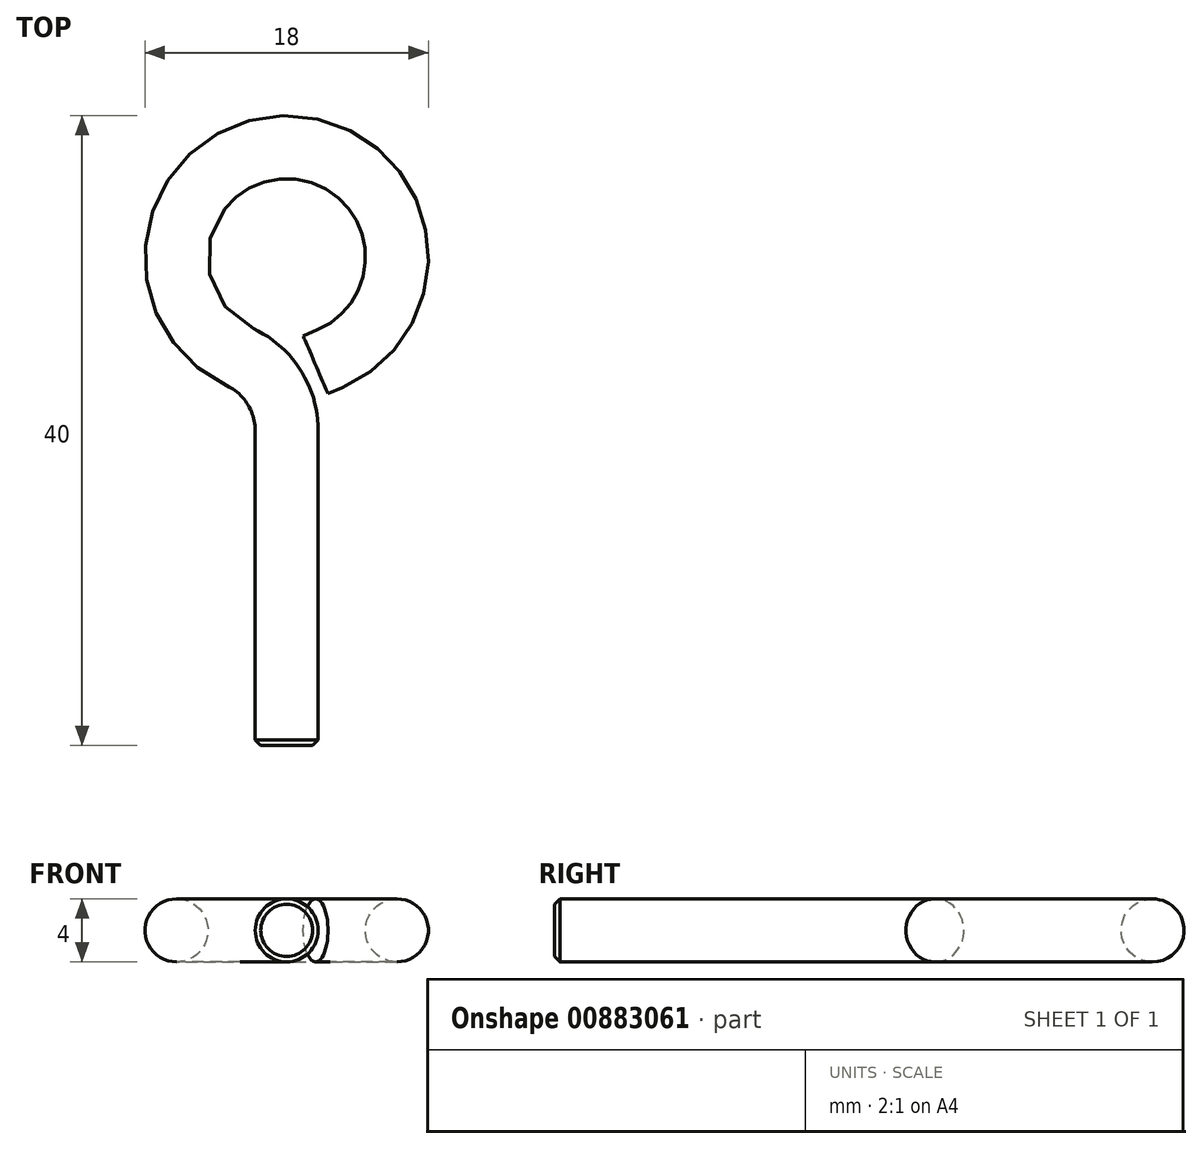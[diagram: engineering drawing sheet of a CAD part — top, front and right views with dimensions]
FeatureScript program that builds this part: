
annotation { "Feature Type Name" : "Feature", "Feature Type Description" : "" }
export const myFeature = defineFeature(function(context is Context, id is Id, definition is map)
    precondition{}
    {
        {
            var Q0;
            Q0=qCreatedBy(makeId("Top.planeOp"),FACE);
            var sketch = newSketch(context, id + "F0", { "sketchPlane" : qUnion([Q0])});
            skArc(sketch, "E0", {"start": v(2.76, 24.57) * mm, "mid": v(0.11, 38) * mm, "end": v(-2.96, 24.66) * mm});
            skLineSegment(sketch, "E1", {"start": v(0, 0) * mm, "end": v(0, 20) * mm});
            skArc(sketch, "E2", {"start": v(0, 20) * mm, "mid": v(-0.8, 22.76) * mm, "end": v(-2.96, 24.66) * mm});
            skLineSegment(sketch, "E3", {"start": v(2.76, 24.57) * mm, "end": v(1.84, 24.17) * mm});
            skSolve(sketch);
        }
        {
            var Q0;
            Q0=qCreatedBy(makeId("Front.planeOp"),FACE);
            var sketch = newSketch(context, id + "F1", { "sketchPlane" : qUnion([Q0])});
            skCircle(sketch, "E4", {"center": v(0, 0) * mm, "radius": 2 * mm});
            skSolve(sketch);
        }
        {
            var Q0;
            Q0=makeQuery(id+"F1.imprint","IMPRINT",FACE,{"disambiguationData":[TD([[makeQuery(id+"F1.imprint","IMPRINT",EDGE,{"derivedFrom":sQuery(id+"F1.wireOp",EDGE,"E4")}),1.0]])]});
            var Q1;
            Q1=sQuery(id+"F0.wireOp",EDGE,"E1");
            var Q2;
            Q2=sQuery(id+"F0.wireOp",EDGE,"E2");
            var Q3;
            Q3=sQuery(id+"F0.wireOp",EDGE,"E0");
            var Q4;
            Q4=sQuery(id+"F0.wireOp",EDGE,"E3");
            sweep(context, id + "F2", {"profiles" : qUnion([Q0]), "path" : qUnion([Q1, Q2, Q3, Q4])});
        }
        {
            var Q0;
            Q0=makeQuery(id+"F2.opSweep","CAP_EDGE",EDGE,{"disambiguationData":[OSD([sQuery(id+"F0.wireOp",VERTEX,"E1.start"),sQuery(id+"F1.wireOp",EDGE,"E4")])],"isStart":true});
            chamfer(context, id + "F3", {"entities" : qUnion([Q0]), "width" : (4 - 3.3) / 2 * mm, "tangentPropagation" : true});
        }
    });
